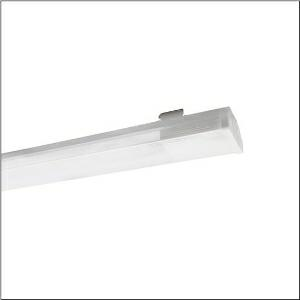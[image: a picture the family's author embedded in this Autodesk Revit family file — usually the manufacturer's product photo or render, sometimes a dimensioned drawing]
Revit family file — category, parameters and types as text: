
# Revit family: modario_31_gen_2_53bm812du4l3d2d_82b8
name_source: partatom
category: Lighting Fixtures
units: mm (PartAtom-declared; Revit-internal decimal feet)

## family parameters
Cut with Voids When Loaded = No
Host = Face
Light Source = No
Part Type = Normal
Room Calculation Point = No
Round Connector Dimension = Use Diameter
Shared = No

## types (1)
- --- (1 x LED, 3710 lm, 21.1 W, 4000K)
    Apparent Load = 21 VA
    CIE Flux Codes = 47 80 95 93 100
    Color Rendering = 80
    Color Temperature = 4000K
    Default Elevation = 1800 mm
    Description = Modario 31 Gen.2, luminaire insert, of sheet steel, coil coated, white, length: 2.392mm, width: 81mm, height: 82mm, 8x system unit, system units: 299mm, LED rated luminous flux: 23.600lm, light colour: 840, SDCM (Standard Deviation of Colour Matching)MacAdam ≤ 3 SDCM (initial), control gear: DALI 2, with plug, 6-pole, with phase selection, mains connection: 220..240V, AC/DC, 0/50..60Hz, rated input power: 128W, for central battery installations according to EN 60598-2-22, for emergency light function, without changeover relay, through-wiring accessed according to module size, primary optical cover: cover, of PMMA, light emission: direct distribution, primary light characteristic: symmetric, protection rating (complete): IP20, protection rating (LED compartment): IP50, insulation class (complete): insulation class I (protective earthing), certification: CE, ENEC, VDE, UKCA, impact resistance: IK03, permissible ambient temperature for indoor applications: -40..+35°C, standard: EN 60598-2-22, corresponds to IFS (International Featured Standards) requirements for safety and quality in the food industry, reducing of maximum allowable ambient temperature of 5°C with ceiling mounting, IP40 when using the optional accessory 5TP9018, packaging unit: 1 piece
    Height = 92 mm
    Lamp = 1 x LED
    Lamp Light Flux = 3710 lm
    Lamp Power = 21.1 W
    Lamp count = 1
    Length = 2392 mm
    Luminous efficacy = 176 lm/W
    Manufacturer = Siteco
    ModVariant = No
    Model = 53BM812DU4L3D2D
    Mounting Place = Ceiling
    Mounting Type = Pendant
    Number of Poles = 1
    OnlyDefault = Yes
    Power Factor = 1
    Product Name = Modario 31 Gen.2
    Product group = luminaire insert | ceiling pendant
    ProductGroupID = 901
    Protection Class = Protection class I
    Protection Degree = IP 20
    RLX_Detail_Level = 1
    RLX_Emergency_Light_Flux = 0 lm
    RLX_Emergency_Type = 0
    RLX_Emergency_Type_DB = No
    RlxData = <blob elided: 39097 chars, md5=88ddb57a>
    Socket = socket
    Standby Power = 0 W
    System Light Flux = 3710 lm
    System Power = 21 W
    Type Comments = : DC mode (central or group accumulator) initial emergency light level
    Type Image = l_1341883.jpg
    URL = http://relux.com
    VarID = @adj_049871
    Voltage = 0 V
    Weight = 0.00 kg
    Width = 81 mm

## geometry (parser evidence)
native form markers: Blend x4, Sweep x10
no freeform markers — native parametric forms only
